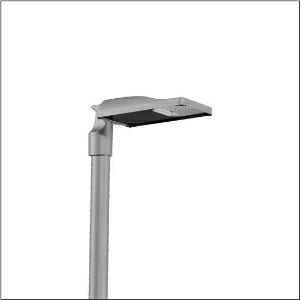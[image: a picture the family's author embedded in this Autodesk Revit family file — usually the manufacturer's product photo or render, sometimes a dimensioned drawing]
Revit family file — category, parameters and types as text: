
# Revit family: streetlight_sl_31_micro___st1_0a_5xh1d71b08ca_ebbd
name_source: partatom
category: Lighting Fixtures
units: mm (PartAtom-declared; Revit-internal decimal feet)

## family parameters
Cut with Voids When Loaded = No
Host = Face
Light Source = No
Part Type = Normal
Room Calculation Point = No
Round Connector Dimension = Use Diameter
Shared = No

## types (1)
- --- (1 x LED, 1170 lm, 10.3 W, 2200K)
    Apparent Load = 10 VA
    CIE Flux Codes = 37 72 97 100 100
    Color Rendering = 70
    Color Temperature = 2200K
    Default Elevation = 1800 mm
    Description = Streetlight SL 31 micro Easy, LST, Desk-Remote mast luminaire for post-top, side-entry; light control with lens of PMMA; light distribution: ST1.0a, direct asymmetric distribution, for standard-compliant lighting for roads and squares; LED: luminous flux: 1.170lm, light colour: 722, colour temperature: 2200K; luminous efficacy: 113,6lm/W; control: pre-setting: linear dimming characteristic, flexible luminous flux parameterisation, time-dependent luminous flux control, constant luminous flux control, power reduction, intelligent temperature release in ECG and LED module, overheat protection; luminaire housing, of diecast aluminium, Siteco® metallic grey (DB 702S), corrosivity category C5 high according to DIN EN ISO 12944; cover of toughened safety glass, transparent, mast flange of diecast aluminium, Siteco® metallic grey (DB 702S), spigot size: 76/60mm, mast flange included unmounted; with cable H07RN-F 3x 1.5mm², cable length: 5,5m, connection cable pre-assembled; mains connection: 220..240V, AC, 50/60Hz; power consumption (at start of service life): 10,3W / (at end of service life): 10,6W / (with reduced operation 50%): 5,3W; protection rating (complete): IP66; insulation class (complete): insulation class II (safety insulation); impact resistance: IK10; certification: CE, ENEC, ENEC+, VDE, UKCA; permissible operating ambient temperature for outdoor applications: -40..+50°C; packaging unit: 1 piece

Light Distribution: ST1.0a
    Height = 76 mm
    Lamp = 1 x LED
    Lamp Light Flux = 1170 lm
    Lamp Power = 10.3 W
    Lamp count = 1
    Length = 467 mm
    Luminous efficacy = 114 lm/W
    Manufacturer = Siteco
    ModVariant = No
    Model = 5XH1D71B08CA
    Number of Poles = 1
    OnlyDefault = Yes
    Power Factor = 1
    Product Name = Streetlight SL 31 micro | ST1.0a
    Product group = mast luminaire | pylon top
    ProductGroupID = 6100
    Protection Class = Protection class II
    Protection Degree = IP 66
    RLX_Detail_Level = 1
    RLX_Emergency_Light_Flux = 0 lm
    RLX_Emergency_Type = 0
    RLX_Emergency_Type_DB = No
    RlxData = <blob elided: 22457 chars, md5=454655db>
    Socket = socket
    Standby Power = 0 W
    System Light Flux = 1170 lm
    System Power = 10 W
    Type Comments = factory setting: luminous flux: 100 % | dim-lin: 254 | 386 mA
    Type Image = l_1300309.jpg
    URL = http://relux.com
    VarID = @adj_008977
    Voltage = 0 V
    Weight = 0.00 kg
    Width = 265 mm

## geometry (parser evidence)
native form markers: Blend x4, Sweep x9
no freeform markers — native parametric forms only
